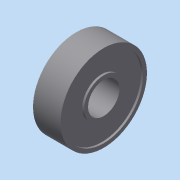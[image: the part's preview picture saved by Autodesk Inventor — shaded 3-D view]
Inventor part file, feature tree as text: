
AUTODESK INVENTOR PART (.ipt)
format: ipt  version: 2014 SP1 (Build 180222100, 222)  size: 103,424 bytes
history: native  units: in
note: dims shown in document units (in); Inventor stores cm internally (conversion verified against a paired STEP export)
features: other x3, sketch x2, plane x1
ambient origin geometry x8: Origin, YZ Plane, XZ Plane, XY Plane, X Axis, Y Axis, Z Axis, Center Point
bodies: Solid1 (feature_tree)
feature tree (6):
  other  "608bearing.ipt"
  other  "Solid1::608bearing.ipt"
  other  "TaggingFeature1"
  sketch  "Sketch1"  dims[d0=0.3937in]
  sketch  "Sketch2"  dims[d1=0.8661in d2=0.2756in d3=0.0in d4=0.0394in d5=0.0394in d6=0.0197in d7=0.0in]
  plane  "Work Plane1"
